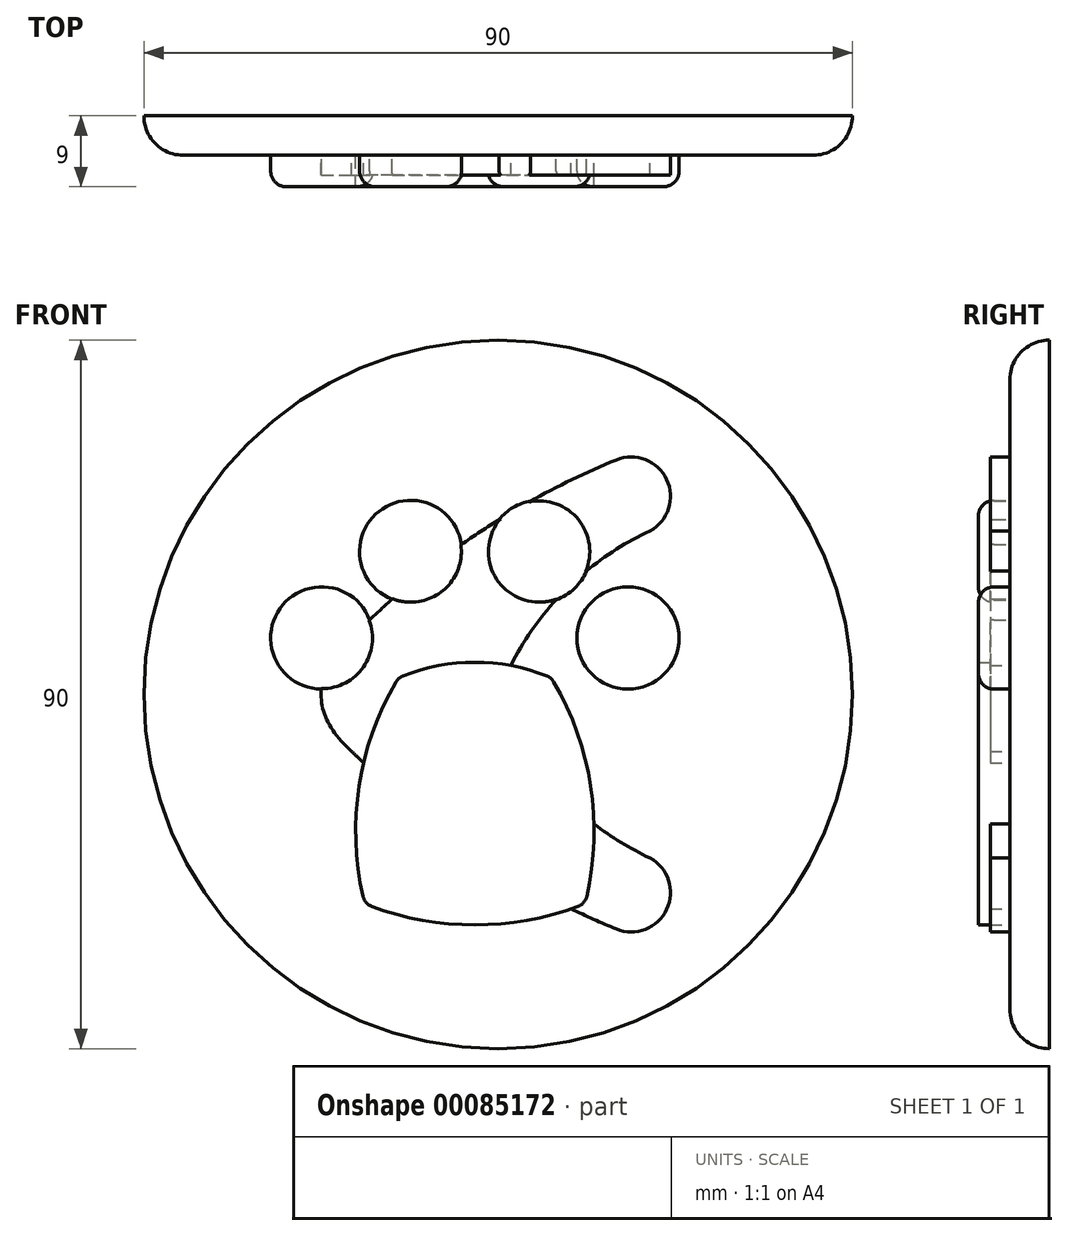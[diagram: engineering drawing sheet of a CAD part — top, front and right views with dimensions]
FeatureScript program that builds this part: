
annotation { "Feature Type Name" : "Feature", "Feature Type Description" : "" }
export const myFeature = defineFeature(function(context is Context, id is Id, definition is map)
    precondition{}
    {
        {
            var Q0;
            Q0=qCreatedBy(makeId("Front.planeOp"),FACE);
            var sketch = newSketch(context, id + "F0", { "sketchPlane" : qUnion([Q0])});
            skLineSegment(sketch, "E0", {"start": v(0, 0) * mm, "end": v(-25, 0) * mm, "construction": true});
            skLineSegment(sketch, "E1", {"start": v(-25, 0) * mm, "end": v(-12.1, 15.38) * mm, "construction": true});
            skLineSegment(sketch, "E2", {"start": v(-25, 0) * mm, "end": v(0, -29.8) * mm, "construction": true});
            skLineSegment(sketch, "E3", {"start": v(-37.5, 0) * mm, "end": v(-37.5, 51.52) * mm, "construction": true});
            skPoint(sketch, "E4.third.point", {"position": v(35.52, 30.3) * mm});
            skCircle(sketch, "E5", {"center": v(52.2, 0) * mm, "radius": 26.18 * mm, "construction": true});
            skEllipticalArc(sketch, "E6.trimOffspring", {"construction": true});
            skLineSegment(sketch, "E7", {"start": v(-25, 0) * mm, "end": v(-33.6, -7.22) * mm, "construction": true});
            skLineSegment(sketch, "E8.MirrorCS", {"start": v(-25, 0) * mm, "end": v(-33.6, 7.22) * mm, "construction": true});
            skArc(sketch, "E9", {"start": v(-33.6, -7.22) * mm, "mid": v(-17.95, -20.22) * mm, "end": v(0, -29.8) * mm});
            skArc(sketch, "E10.MirrorCS", {"start": v(-33.6, 7.22) * mm, "mid": v(-17.95, 20.22) * mm, "end": v(0, 29.8) * mm});
            skLineSegment(sketch, "E11", {"start": v(0, -29.8) * mm, "end": v(3.78, -20.54) * mm, "construction": true});
            skArc(sketch, "E12", {"start": v(0, -29.8) * mm, "mid": v(6.4, -27.3) * mm, "end": v(4.28, -20.77) * mm});
            skLineSegment(sketch, "E13", {"start": v(0, 29.8) * mm, "end": v(3.78, 20.54) * mm, "construction": true});
            skArc(sketch, "E14", {"start": v(4.28, 20.77) * mm, "mid": v(6.4, 27.3) * mm, "end": v(0, 29.8) * mm});
            skLineSegment(sketch, "E15", {"start": v(-15, -10.1) * mm, "end": v(-15, 10.1) * mm, "construction": true});
            skPoint(sketch, "E16.second.point", {"position": v(-15, 0) * mm});
            skEllipticalArc(sketch, "E17.trimOffspring", {});
            skArc(sketch, "E18", {"start": v(4.28, 20.77) * mm, "mid": v(-7.4, 12.28) * mm, "end": v(-15, 0) * mm});
            skPoint(sketch, "E18.third.point", {"position": v(10.4, 23) * mm});
            skArc(sketch, "E19.MirrorCS", {"start": v(4.28, -20.77) * mm, "mid": v(-7.4, -12.28) * mm, "end": v(-15, 0) * mm});
            const initialGuessF0  = {"E6.trimOffspring": [-0.0375, 0, 0.7242400212320117, 0.6895479618169105, 0.05177841447674814, 0.006, 4.833501710182894, 5.264286936313878], "E17.trimOffspring": [0, 0, -1, 0, 0.0375, 0.01625, 5.823053804272296, 0.46013150290731647]};
            skSetInitialGuess(sketch, initialGuessF0);
            skSolve(sketch);
        }
        {
            var Q0;
            Q0=qCreatedBy(makeId("Front.planeOp"),FACE);
            var sketch = newSketch(context, id + "F7", { "sketchPlane" : qUnion([Q0])});
            skCircle(sketch, "E20", {"center": v(-15, 0) * mm, "radius": 45 * mm});
            skSolve(sketch);
        }
        {
            var Q0;
            Q0 = qSketchRegion(id + "F0", true);
            extrude(context, id + "F1", {"entities" : qUnion([Q0]), "depth" : 5 * mm});
        }
        {
            var Q0;
            Q0 = qSketchRegion(id + "F7", true);
            extrude(context, id + "F2", {"entities" : qUnion([Q0]), "operationType" : NewBodyOperationType.ADD, "endBound" : BoundingType.SYMMETRIC, "depth" : 5 * mm});
        }
        {
            var Q0;
            Q0=makeQuery(id+"F2.opExtrude","CAP_FACE",FACE,{"disambiguationData":[OSD([sQuery(id+"F7.wireOp",EDGE,"E20")])],"isStart":false});
            var sketch = newSketch(context, id + "F3", { "sketchPlane" : qUnion([Q0])});
            skCircle(sketch, "E21", {"center": v(-17.95, -12.28) * mm, "radius": 17.52 * mm, "construction": true});
            skPoint(sketch, "E21.centerSnap0", {"position": v(-7.4, -12.28) * mm});
            skPoint(sketch, "E21.centerSnap1", {"position": v(-17.95, -20.22) * mm});
            skLineSegment(sketch, "E22", {"start": v(0, -29.8) * mm, "end": v(-88.49, -29.8) * mm, "construction": true});
            skLineSegment(sketch, "E23", {"start": v(-17.95, -12.28) * mm, "end": v(-40.23, 10) * mm, "construction": true});
            skLineSegment(sketch, "E24", {"start": v(-17.95, -12.28) * mm, "end": v(-17.95, 39.25) * mm, "construction": true});
            skLineSegment(sketch, "E25", {"start": v(-17.95, -12.28) * mm, "end": v(4.32, 10) * mm, "construction": true});
            skCircle(sketch, "E26", {"center": v(-17.95, -12.28) * mm, "radius": 31.5 * mm, "construction": true});
            skLineSegment(sketch, "E27", {"start": v(-17.95, -12.28) * mm, "end": v(-26.1, 18.15) * mm, "construction": true});
            skCircle(sketch, "E28", {"center": v(-26.1, 18.15) * mm, "radius": 6.5 * mm});
            skCircle(sketch, "E29.MirrorC", {"center": v(-9.8, 18.15) * mm, "radius": 6.5 * mm});
            skCircle(sketch, "E30", {"center": v(-17.95, -12.28) * mm, "radius": 27.5 * mm, "construction": true});
            skCircle(sketch, "E31", {"center": v(1.5, 7.17) * mm, "radius": 6.5 * mm});
            skCircle(sketch, "E32", {"center": v(-37.4, 7.17) * mm, "radius": 6.5 * mm});
            skLineSegment(sketch, "E33", {"start": v(-17.95, -12.28) * mm, "end": v(-17.95, -29.8) * mm, "construction": true});
            skEllipse(sketch, "E34", {"center": v(-17.95, -12.28) * mm, "majorRadius": 13 * mm, "minorRadius": 6.75 * mm, "majorAxis": v(0, -1), "construction": true});
            skLineSegment(sketch, "E35", {"start": v(-17.95, -25.28) * mm, "end": v(-5.45, -25.28) * mm, "construction": true});
            skLineSegment(sketch, "E36.MirrorCS", {"start": v(-17.95, -25.28) * mm, "end": v(-30.45, -25.28) * mm, "construction": true});
            skLineSegment(sketch, "E37", {"start": v(-17.95, 0.72) * mm, "end": v(-26.45, 0.72) * mm, "construction": true});
            skLineSegment(sketch, "E38.MirrorCS", {"start": v(-17.95, 0.72) * mm, "end": v(-9.45, 0.72) * mm, "construction": true});
            skLineSegment(sketch, "E39", {"start": v(-26.45, 0.72) * mm, "end": v(-30.45, -25.28) * mm, "construction": true});
            skLineSegment(sketch, "E40", {"start": v(-9.45, 0.72) * mm, "end": v(-5.45, -25.28) * mm, "construction": true});
            skArc(sketch, "E41", {"start": v(-27.1, 2.35) * mm, "mid": v(-27.6, 2.05) * mm, "end": v(-27.96, 1.6) * mm});
            skArc(sketch, "E42", {"start": v(-32.16, -25.67) * mm, "mid": v(-31.77, -26.43) * mm, "end": v(-31.07, -26.92) * mm});
            skArc(sketch, "E43", {"start": v(-4.84, -26.92) * mm, "mid": v(-4.14, -26.43) * mm, "end": v(-3.75, -25.67) * mm});
            skArc(sketch, "E44", {"start": v(-7.94, 1.6) * mm, "mid": v(-8.32, 2.05) * mm, "end": v(-8.81, 2.35) * mm});
            skArc(sketch, "E45", {"start": v(-27.96, 1.6) * mm, "mid": v(-32.66, -11.63) * mm, "end": v(-32.16, -25.67) * mm});
            skArc(sketch, "E46.MirrorCS", {"start": v(-7.94, 1.6) * mm, "mid": v(-3.25, -11.63) * mm, "end": v(-3.75, -25.67) * mm});
            skArc(sketch, "E47", {"start": v(-31.07, -26.92) * mm, "mid": v(-17.95, -29.28) * mm, "end": v(-4.84, -26.92) * mm});
            skArc(sketch, "E48", {"start": v(-8.81, 2.35) * mm, "mid": v(-17.95, 4.08) * mm, "end": v(-27.1, 2.35) * mm});
            skSolve(sketch);
        }
        {
            var Q0;
            Q0 = qSketchRegion(id + "F3", true);
            extrude(context, id + "F4", {"entities" : qUnion([Q0]), "operationType" : NewBodyOperationType.ADD, "depth" : 4 * mm});
        }
        {
            var Q0;
            Q0=makeQuery(id+"F2.opExtrude","CAP_EDGE",EDGE,{"disambiguationData":[OSD([sQuery(id+"F7.wireOp",EDGE,"E20")])],"isStart":false});
            fillet(context, id + "F5", {"entities" : qUnion([Q0]), "radius" : 5 * mm, "tangentPropagation" : true, "allowEdgeOverflow" : false});
        }
        {
            var Q0;
            Q0=makeQuery(id+"F4.opExtrude","CAP_FACE",FACE,{"disambiguationData":[OSD([sQuery(id+"F3.wireOp",EDGE,"E31")])],"isStart":false});
            var Q1;
            Q1=makeQuery(id+"F4.opExtrude","CAP_FACE",FACE,{"disambiguationData":[OSD([sQuery(id+"F3.wireOp",EDGE,"E29.MirrorC")])],"isStart":false});
            var Q2;
            Q2=makeQuery(id+"F4.opExtrude","CAP_FACE",FACE,{"disambiguationData":[OSD([sQuery(id+"F3.wireOp",EDGE,"E28")])],"isStart":false});
            var Q3;
            Q3=makeQuery(id+"F4.opExtrude","CAP_FACE",FACE,{"disambiguationData":[OSD([sQuery(id+"F3.wireOp",EDGE,"E32")])],"isStart":false});
            fillet(context, id + "F6", {"entities" : qUnion([Q0, Q1, Q2, Q3]), "radius" : 2 * mm, "tangentPropagation" : true, "allowEdgeOverflow" : false});
        }
    });
